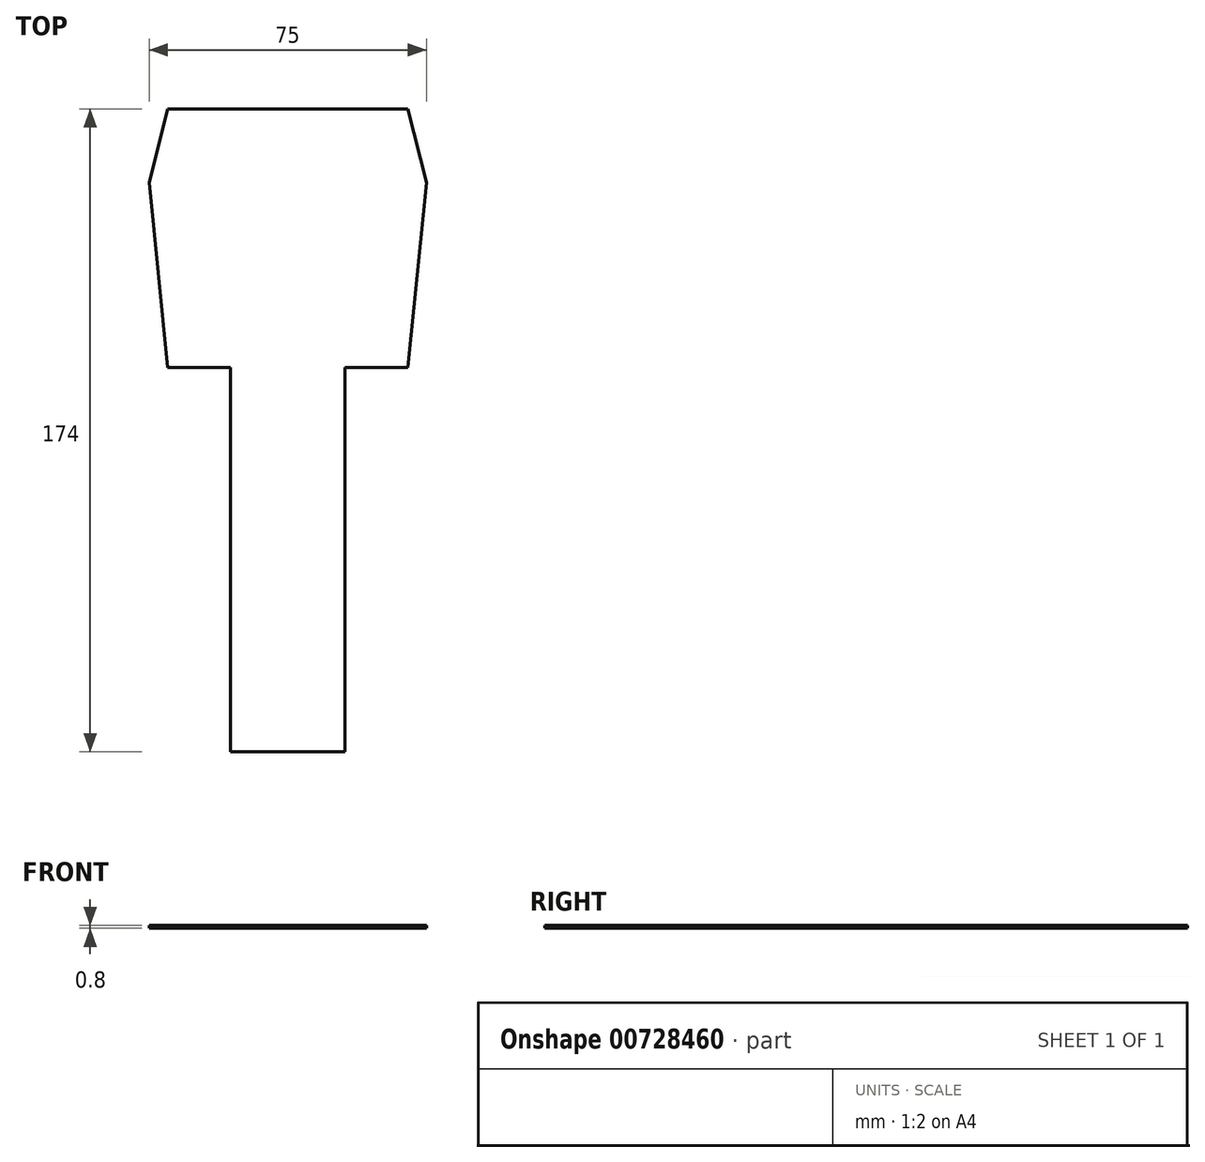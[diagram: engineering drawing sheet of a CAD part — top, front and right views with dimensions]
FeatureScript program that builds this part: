
annotation { "Feature Type Name" : "Feature", "Feature Type Description" : "" }
export const myFeature = defineFeature(function(context is Context, id is Id, definition is map)
    precondition{}
    {
        {
            var Q0;
            Q0=qCreatedBy(makeId("Top.planeOp"),FACE);
            var sketch = newSketch(context, id + "F0", { "sketchPlane" : qUnion([Q0])});
            skLineSegment(sketch, "E0.bottom", {"start": v(8.5, -35) * mm, "end": v(-8.5, -35) * mm});
            skLineSegment(sketch, "E0.top", {"start": v(8.5, 35) * mm, "end": v(-8.5, 35) * mm});
            skLineSegment(sketch, "E0.right", {"start": v(-8.5, -35) * mm, "end": v(-8.5, 35) * mm});
            skPoint(sketch, "E0.middle", {"position": v(0, 0) * mm});
            skLineSegment(sketch, "E1", {"start": v(8.5, 35) * mm, "end": v(13.5, 15) * mm});
            skLineSegment(sketch, "E2", {"start": v(13.5, 15) * mm, "end": v(8.5, -35) * mm});
            skLineSegment(sketch, "E3.bottom", {"start": v(-8.5, 35) * mm, "end": v(-39.5, 35) * mm});
            skLineSegment(sketch, "E3.top", {"start": v(-8.5, -35) * mm, "end": v(-39.5, -35) * mm});
            skLineSegment(sketch, "E3.left", {"start": v(-8.5, 35) * mm, "end": v(-8.5, -35) * mm});
            skLineSegment(sketch, "E3.right", {"start": v(-39.5, 35) * mm, "end": v(-39.5, -35) * mm});
            skLineSegment(sketch, "E4", {"start": v(-39.5, 35) * mm, "end": v(-56.5, 35) * mm});
            skLineSegment(sketch, "E5", {"start": v(-56.5, 35) * mm, "end": v(-61.5, 15) * mm});
            skLineSegment(sketch, "E6", {"start": v(-61.5, 15) * mm, "end": v(-56.5, -35) * mm});
            skLineSegment(sketch, "E7", {"start": v(-56.5, -35) * mm, "end": v(-39.5, -35) * mm});
            skLineSegment(sketch, "E8.bottom", {"start": v(-39.5, -35) * mm, "end": v(-8.5, -35) * mm});
            skLineSegment(sketch, "E8.top", {"start": v(-39.5, -139) * mm, "end": v(-8.5, -139) * mm});
            skLineSegment(sketch, "E8.left", {"start": v(-39.5, -35) * mm, "end": v(-39.5, -139) * mm});
            skLineSegment(sketch, "E8.right", {"start": v(-8.5, -35) * mm, "end": v(-8.5, -139) * mm});
            skLineSegment(sketch, "E9", {"start": v(-39.5, -52) * mm, "end": v(-8.5, -52) * mm});
            skPoint(sketch, "E9.endSnap0", {"position": v(-8.5, -87) * mm});
            skLineSegment(sketch, "E10", {"start": v(-39.5, -102) * mm, "end": v(-8.5, -102) * mm});
            skLineSegment(sketch, "E11", {"start": v(-39.5, -122) * mm, "end": v(-8.5, -122) * mm});
            skSolve(sketch);
        }
        {
            var Q0;
            Q0 = qSketchRegion(id + "F0", true);
            extrude(context, id + "F1", {"entities" : qUnion([Q0]), "endBound" : BoundingType.SYMMETRIC, "depth" : 0.8 * mm, "offsetDistance" : 25 * mm});
        }
    });
